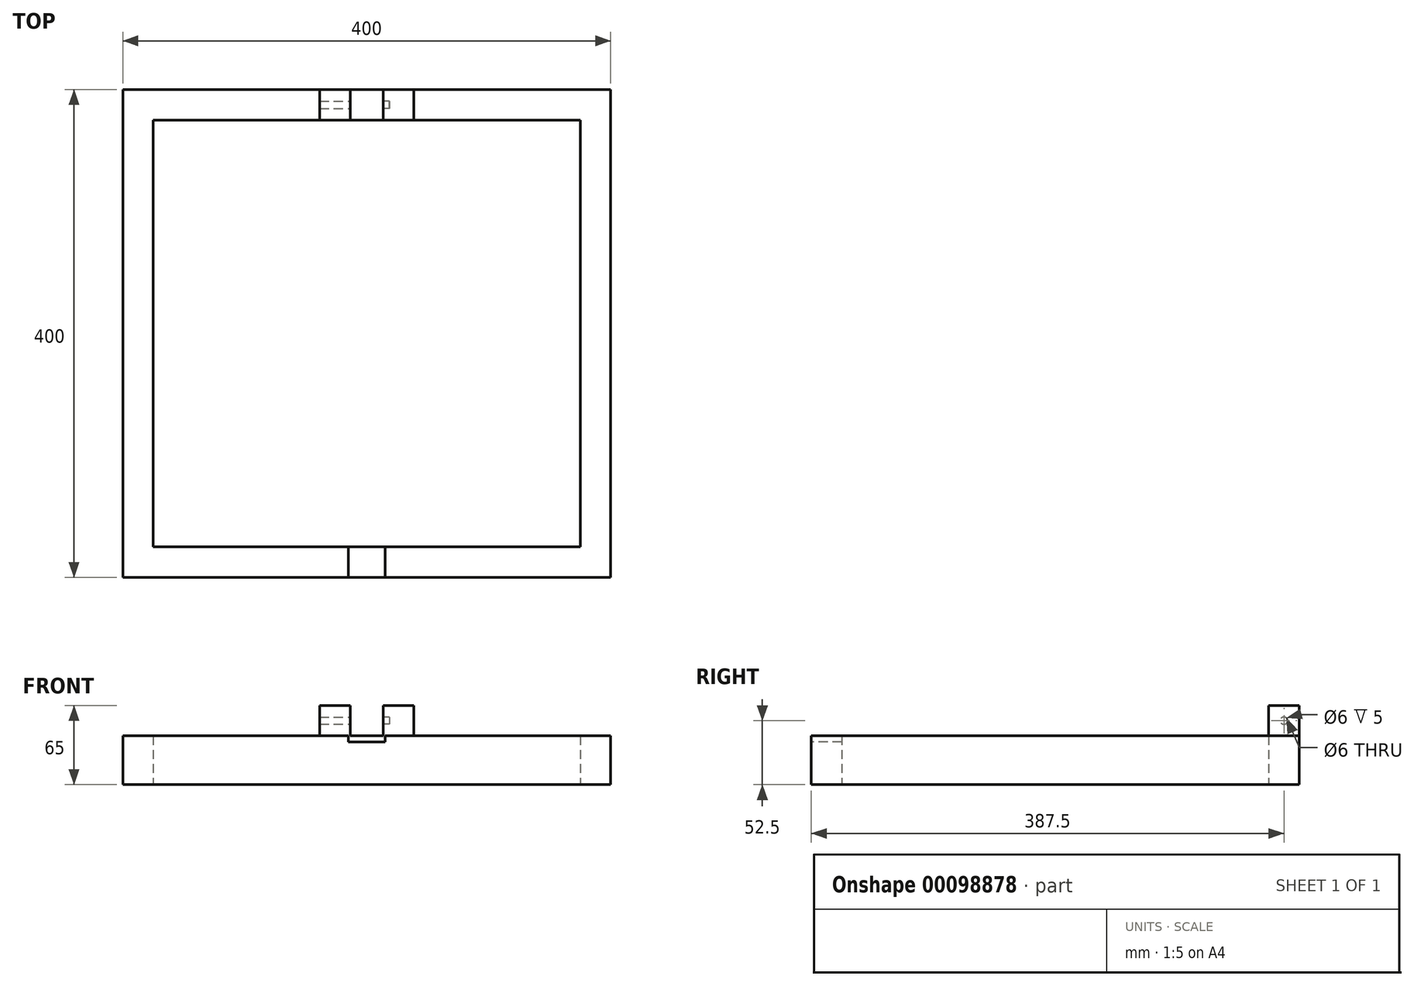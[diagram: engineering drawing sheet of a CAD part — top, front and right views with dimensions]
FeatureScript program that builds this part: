
annotation { "Feature Type Name" : "Feature", "Feature Type Description" : "" }
export const myFeature = defineFeature(function(context is Context, id is Id, definition is map)
    precondition{}
    {
        {
            var Q0;
            Q0=qCreatedBy(makeId("Top.planeOp"),FACE);
            var sketch = newSketch(context, id + "F0", { "sketchPlane" : qUnion([Q0])});
            skLineSegment(sketch, "E0.bottom", {"start": v(200, 200) * mm, "end": v(-200, 200) * mm});
            skLineSegment(sketch, "E0.top", {"start": v(200, -200) * mm, "end": v(-200, -200) * mm});
            skLineSegment(sketch, "E0.left", {"start": v(200, 200) * mm, "end": v(200, -200) * mm});
            skLineSegment(sketch, "E0.right", {"start": v(-200, 200) * mm, "end": v(-200, -200) * mm});
            skPoint(sketch, "E0.middle", {"position": v(0, 0) * mm});
            skLineSegment(sketch, "E1.0", {"start": v(175, 175) * mm, "end": v(175, -175) * mm});
            skLineSegment(sketch, "E1.1", {"start": v(175, 175) * mm, "end": v(-175, 175) * mm});
            skLineSegment(sketch, "E1.2", {"start": v(-175, 175) * mm, "end": v(-175, -175) * mm});
            skLineSegment(sketch, "E1.3", {"start": v(175, -175) * mm, "end": v(-175, -175) * mm});
            skSolve(sketch);
        }
        {
            var Q0;
            Q0=makeQuery(id+"F0.imprint","IMPRINT",FACE,{"disambiguationData":[TD([[makeQuery(id+"F0.imprint","IMPRINT",EDGE,{"derivedFrom":sQuery(id+"F0.wireOp",EDGE,"E0.bottom")}),1.0]])]});
            extrude(context, id + "F1", {"entities" : qUnion([Q0]), "depth" : 40 * mm});
        }
        {
            var Q0;
            Q0=makeQuery(id+"F1.opExtrude","SWEPT_FACE",FACE,{"disambiguationData":[OSD([sQuery(id+"F0.wireOp",EDGE,"E0.top")])]});
            var sketch = newSketch(context, id + "F2", { "sketchPlane" : qUnion([Q0])});
            skLineSegment(sketch, "E2.left", {"start": v(15, 35) * mm, "end": v(15, 40) * mm});
            skLineSegment(sketch, "E2.right", {"start": v(-15, 35) * mm, "end": v(-15, 40) * mm});
            skPoint(sketch, "E2.middle", {"position": v(0, 40) * mm});
            skLineSegment(sketch, "E3", {"start": v(-15, 40) * mm, "end": v(15, 40) * mm});
            skLineSegment(sketch, "E4", {"start": v(-15, 40) * mm, "end": v(-15, 35) * mm});
            skLineSegment(sketch, "E5", {"start": v(-15, 35) * mm, "end": v(15, 35) * mm});
            skSolve(sketch);
        }
        {
            var Q0;
            Q0 = qSketchRegion(id + "F2", true);
            extrude(context, id + "F3", {"entities" : qUnion([Q0]), "operationType" : NewBodyOperationType.REMOVE, "endBound" : BoundingType.UP_TO_NEXT, "oppositeDirection" : true, "depth" : 25 * mm});
        }
        {
            var Q0;
            Q0=makeQuery(id+"F1.opExtrude","CAP_FACE",FACE,{"disambiguationData":[OSD([sQuery(id+"F0.wireOp",EDGE,"E0.bottom"),sQuery(id+"F0.wireOp",EDGE,"E0.top"),sQuery(id+"F0.wireOp",EDGE,"E0.left"),sQuery(id+"F0.wireOp",EDGE,"E0.right"),sQuery(id+"F0.wireOp",EDGE,"E1.0"),sQuery(id+"F0.wireOp",EDGE,"E1.1"),sQuery(id+"F0.wireOp",EDGE,"E1.2"),sQuery(id+"F0.wireOp",EDGE,"E1.3")])],"isStart":false});
            var sketch = newSketch(context, id + "F4", { "sketchPlane" : qUnion([Q0])});
            skLineSegment(sketch, "E6.bottom", {"start": v(13.5, 200) * mm, "end": v(-13.5, 200) * mm});
            skLineSegment(sketch, "E6.top", {"start": v(13.5, 175) * mm, "end": v(-13.5, 175) * mm});
            skLineSegment(sketch, "E6.left", {"start": v(13.5, 200) * mm, "end": v(13.5, 175) * mm});
            skLineSegment(sketch, "E6.right", {"start": v(-13.5, 200) * mm, "end": v(-13.5, 175) * mm});
            skPoint(sketch, "E6.middle", {"position": v(0, 187.5) * mm});
            skLineSegment(sketch, "E7.bottom", {"start": v(-13.5, 200) * mm, "end": v(-38.5, 200) * mm});
            skLineSegment(sketch, "E7.top", {"start": v(-13.5, 175) * mm, "end": v(-38.5, 175) * mm});
            skLineSegment(sketch, "E7.right", {"start": v(-38.5, 200) * mm, "end": v(-38.5, 175) * mm});
            skLineSegment(sketch, "E8.bottom", {"start": v(13.5, 200) * mm, "end": v(38.5, 200) * mm});
            skLineSegment(sketch, "E8.top", {"start": v(13.5, 175) * mm, "end": v(38.5, 175) * mm});
            skLineSegment(sketch, "E8.right", {"start": v(38.5, 200) * mm, "end": v(38.5, 175) * mm});
            skPoint(sketch, "E9.orphan", {"position": v(0, 200) * mm});
            skPoint(sketch, "E10.end.orphan", {"position": v(0, 175) * mm});
            skSolve(sketch);
        }
        {
            var Q0;
            Q0=makeQuery(id+"F4.imprint","IMPRINT",FACE,{"disambiguationData":[TD([[makeQuery(id+"F4.imprint","IMPRINT",EDGE,{"derivedFrom":sQuery(id+"F4.wireOp",EDGE,"E7.bottom")}),1.0]])]});
            var Q1;
            Q1=makeQuery(id+"F4.imprint","IMPRINT",FACE,{"disambiguationData":[TD([[makeQuery(id+"F4.imprint","IMPRINT",EDGE,{"derivedFrom":sQuery(id+"F4.wireOp",EDGE,"E8.bottom")}),1.0]])]});
            extrude(context, id + "F5", {"entities" : qUnion([Q0, Q1]), "operationType" : NewBodyOperationType.ADD, "depth" : 25 * mm});
        }
        {
            var Q0;
            Q0=makeQuery(id+"F5.opExtrude","SWEPT_FACE",FACE,{"disambiguationData":[OSD([sQuery(id+"F4.wireOp",EDGE,"E6.left")])]});
            var sketch = newSketch(context, id + "F6", { "sketchPlane" : qUnion([Q0])});
            skCircle(sketch, "E11", {"center": v(-187.5, 52.5) * mm, "radius": 3 * mm});
            skPoint(sketch, "E11.centerSnap0", {"position": v(-175, 52.5) * mm});
            skPoint(sketch, "E11.centerSnap1", {"position": v(-187.5, 65) * mm});
            skSolve(sketch);
        }
        {
            var Q0;
            Q0=makeQuery(id+"F6.imprint","IMPRINT",FACE,{"disambiguationData":[TD([[makeQuery(id+"F6.imprint","IMPRINT",EDGE,{"derivedFrom":sQuery(id+"F6.wireOp",EDGE,"E11")}),1.0]])]});
            extrude(context, id + "F7", {"entities" : qUnion([Q0]), "operationType" : NewBodyOperationType.REMOVE, "oppositeDirection" : true, "depth" : 5 * mm});
        }
        {
            var Q0;
            Q0=makeQuery(id+"F5.opExtrude","SWEPT_FACE",FACE,{"disambiguationData":[OSD([sQuery(id+"F4.wireOp",EDGE,"E6.right")])]});
            var sketch = newSketch(context, id + "F8", { "sketchPlane" : qUnion([Q0])});
            skCircle(sketch, "E12", {"center": v(187.5, 52.5) * mm, "radius": 3 * mm});
            skPoint(sketch, "E12.centerSnap0", {"position": v(200, 52.5) * mm});
            skPoint(sketch, "E12.centerSnap1", {"position": v(187.5, 65) * mm});
            skSolve(sketch);
        }
        {
            var Q0;
            Q0=makeQuery(id+"F8.imprint","IMPRINT",FACE,{"disambiguationData":[TD([[makeQuery(id+"F8.imprint","IMPRINT",EDGE,{"derivedFrom":sQuery(id+"F8.wireOp",EDGE,"E12")}),1.0]])]});
            extrude(context, id + "F9", {"entities" : qUnion([Q0]), "operationType" : NewBodyOperationType.REMOVE, "endBound" : BoundingType.UP_TO_NEXT, "oppositeDirection" : true, "depth" : 25 * mm});
        }
    });
